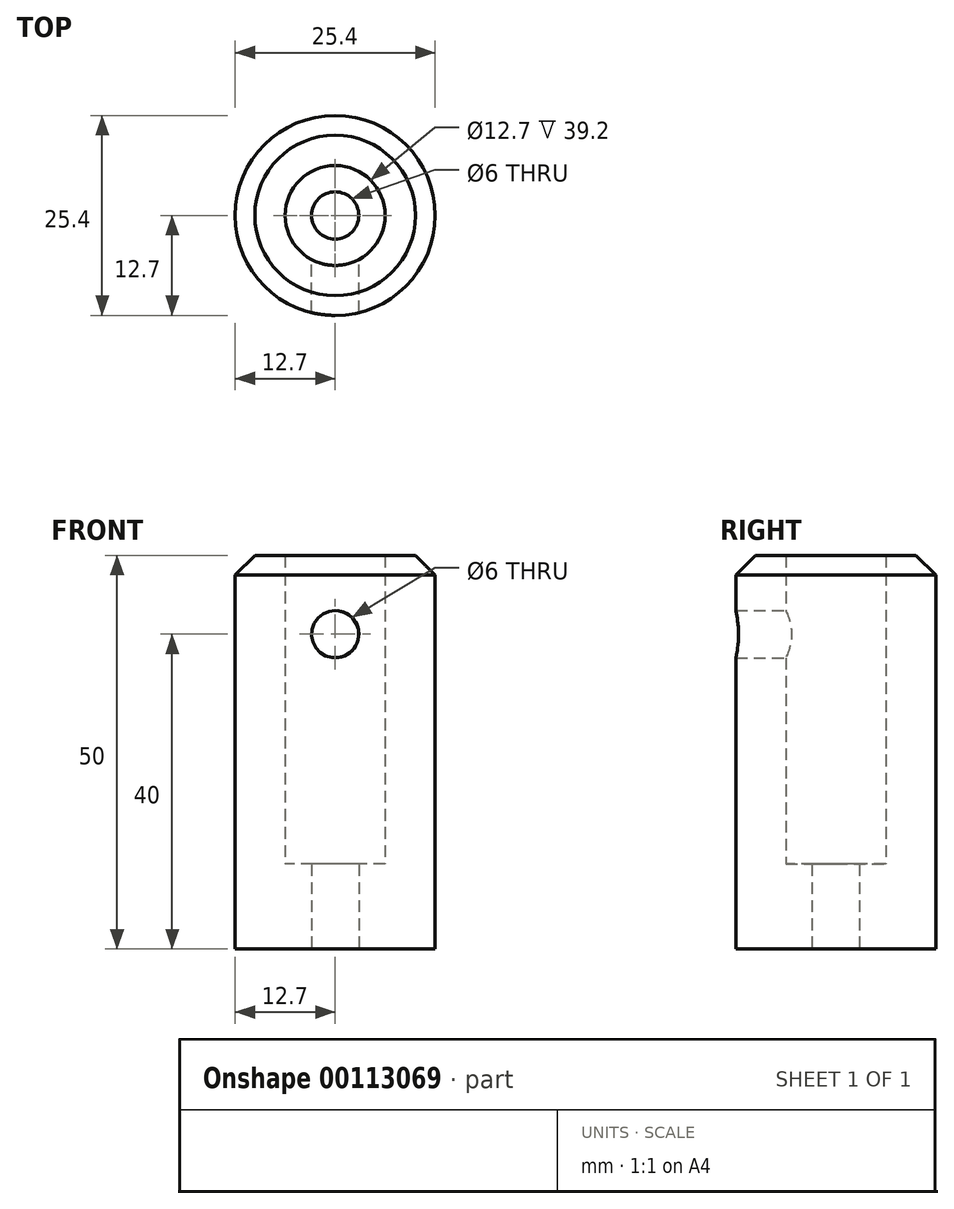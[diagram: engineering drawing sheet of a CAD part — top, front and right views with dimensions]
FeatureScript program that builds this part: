
annotation { "Feature Type Name" : "Feature", "Feature Type Description" : "" }
export const myFeature = defineFeature(function(context is Context, id is Id, definition is map)
    precondition{}
    {
        {
            var Q0;
            Q0=qCreatedBy(makeId("Top.planeOp"),FACE);
            var sketch = newSketch(context, id + "F0", { "sketchPlane" : qUnion([Q0])});
            skCircle(sketch, "E0", {"center": v(0, 0) * mm, "radius": 12.7 * mm});
            skCircle(sketch, "E1", {"center": v(0, 0) * mm, "radius": 6.35 * mm});
            skCircle(sketch, "E2", {"center": v(0, 0) * mm, "radius": 3 * mm});
            skSolve(sketch);
        }
        {
            var Q0;
            Q0=makeQuery(id+"F0.imprint","IMPRINT",FACE,{"disambiguationData":[TD([[makeQuery(id+"F0.imprint","IMPRINT",EDGE,{"derivedFrom":sQuery(id+"F0.wireOp",EDGE,"E0")}),1.0]])]});
            extrude(context, id + "F1", {"entities" : qUnion([Q0]), "depth" : 50 * mm});
        }
        {
            var Q0;
            Q0=makeQuery(id+"F0.imprint","IMPRINT",FACE,{"disambiguationData":[TD([[makeQuery(id+"F0.imprint","IMPRINT",EDGE,{"derivedFrom":sQuery(id+"F0.wireOp",EDGE,"E1")}),1.0]])]});
            extrude(context, id + "F2", {"entities" : qUnion([Q0]), "operationType" : NewBodyOperationType.ADD, "depth" : 10.8 * mm});
        }
        {
            var Q0;
            Q0=makeQuery(id+"F1.opExtrude","CAP_EDGE",EDGE,{"disambiguationData":[OSD([sQuery(id+"F0.wireOp",EDGE,"E0")])],"isStart":false});
            chamfer(context, id + "F3", {"entities" : qUnion([Q0]), "width" : 2.5 * mm, "tangentPropagation" : true});
        }
        {
            var Q0;
            Q0=qCreatedBy(makeId("Front.planeOp"),FACE);
            var sketch = newSketch(context, id + "F4", { "sketchPlane" : qUnion([Q0])});
            skCircle(sketch, "E3", {"center": v(0, 40) * mm, "radius": 3 * mm});
            skSolve(sketch);
        }
        {
            var Q0;
            Q0=makeQuery(id+"F4.imprint","IMPRINT",FACE,{"disambiguationData":[TD([[makeQuery(id+"F4.imprint","IMPRINT",EDGE,{"derivedFrom":sQuery(id+"F4.wireOp",EDGE,"E3")}),1.0]])]});
            extrude(context, id + "F5", {"entities" : qUnion([Q0]), "operationType" : NewBodyOperationType.REMOVE, "depth" : 25 * mm});
        }
    });
